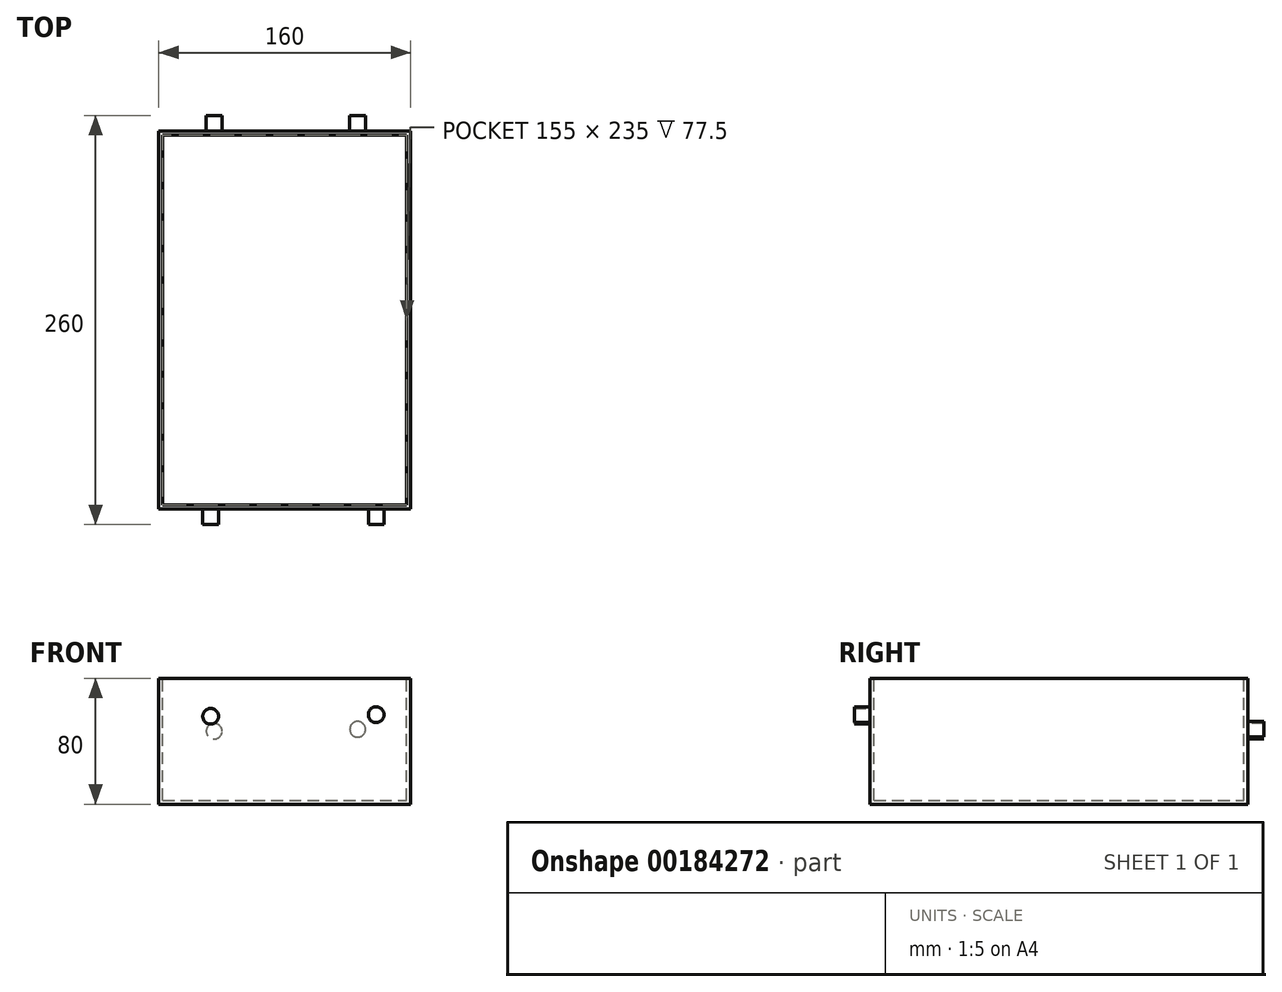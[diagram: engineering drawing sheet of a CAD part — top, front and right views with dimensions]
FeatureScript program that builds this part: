
annotation { "Feature Type Name" : "Feature", "Feature Type Description" : "" }
export const myFeature = defineFeature(function(context is Context, id is Id, definition is map)
    precondition{}
    {
        {
            var Q0;
            Q0=qCreatedBy(makeId("Front.planeOp"),FACE);
            var sketch = newSketch(context, id + "F0", { "sketchPlane" : qUnion([Q0])});
            skLineSegment(sketch, "E0.bottom", {"start": v(-80, -40) * mm, "end": v(80, -40) * mm});
            skLineSegment(sketch, "E0.top", {"start": v(-80, 40) * mm, "end": v(80, 40) * mm});
            skLineSegment(sketch, "E0.left", {"start": v(-80, -40) * mm, "end": v(-80, 40) * mm});
            skLineSegment(sketch, "E0.right", {"start": v(80, -40) * mm, "end": v(80, 40) * mm});
            skPoint(sketch, "E0.middle", {"position": v(0, 0) * mm});
            skSolve(sketch);
        }
        {
            var Q0;
            Q0=makeQuery(id+"F0.imprint","IMPRINT",FACE,{"disambiguationData":[TD([[makeQuery(id+"F0.imprint","IMPRINT",EDGE,{"derivedFrom":sQuery(id+"F0.wireOp",EDGE,"E0.bottom")}),1.0]])]});
            var sketch = newSketch(context, id + "F1", { "sketchPlane" : qUnion([Q0])});
            skSolve(sketch);
        }
        {
            var Q0;
            Q0=makeQuery(id+"F1.imprint","IMPRINT",FACE,{"disambiguationData":[TD([[makeQuery(id+"F1.imprint","IMPRINT",EDGE,{"derivedFrom":makeQuery(id+"F0.imprint","IMPRINT",EDGE,{"derivedFrom":sQuery(id+"F0.wireOp",EDGE,"E0.bottom")})}),1.0]])]});
            extrude(context, id + "F2", {"entities" : qUnion([Q0]), "endBound" : BoundingType.SYMMETRIC, "depth" : 240 * mm});
        }
        {
            var Q0;
            Q0=makeQuery(id+"F2.opExtrude","SWEPT_FACE",FACE,{"disambiguationData":[OSD([sQuery(id+"F0.wireOp",EDGE,"E0.left")])]});
            var sketch = newSketch(context, id + "F3", { "sketchPlane" : qUnion([Q0])});
            skSolve(sketch);
        }
        {
            var Q0;
            {var subQ0=sQuery(id+"F0.wireOp",EDGE,"E0.left");Q0=makeQuery(id+"F3.imprint","IMPRINT",FACE,{"disambiguationData":[TD([[makeQuery(id+"F3.imprint","IMPRINT",EDGE,{"derivedFrom":makeQuery(id+"F2.opExtrude","CAP_EDGE",EDGE,{"disambiguationData":[OSD([subQ0])],"isStart":true})}),-1.0]])]});}
            var sketch = newSketch(context, id + "F4", { "sketchPlane" : qUnion([Q0])});
            skSolve(sketch);
        }
        {
            var Q0;
            Q0=makeQuery(id+"F2.opExtrude","SWEPT_FACE",FACE,{"disambiguationData":[OSD([sQuery(id+"F0.wireOp",EDGE,"E0.top")])]});
            shell(context, id + "F5", {"entities" : qUnion([Q0]), "thickness" : 2.5 * mm});
        }
        {
            var Q0;
            Q0=makeQuery(id+"F2.opExtrude","CAP_FACE",FACE,{"disambiguationData":[OSD([sQuery(id+"F0.wireOp",EDGE,"E0.bottom"),sQuery(id+"F0.wireOp",EDGE,"E0.top"),sQuery(id+"F0.wireOp",EDGE,"E0.left"),sQuery(id+"F0.wireOp",EDGE,"E0.right")])],"isStart":false});
            var sketch = newSketch(context, id + "F6", { "sketchPlane" : qUnion([Q0])});
            skCircle(sketch, "E1", {"center": v(-47.01, 15.8) * mm, "radius": 5 * mm});
            skSolve(sketch);
        }
        {
            var Q0;
            Q0=makeQuery(id+"F6.imprint","IMPRINT",FACE,{"disambiguationData":[TD([[makeQuery(id+"F6.imprint","IMPRINT",EDGE,{"derivedFrom":sQuery(id+"F6.wireOp",EDGE,"E1")}),-1.0]])]});
            var sketch = newSketch(context, id + "F7", { "sketchPlane" : qUnion([Q0])});
            skCircle(sketch, "E2", {"center": v(58.14, 16.82) * mm, "radius": 5 * mm});
            skSolve(sketch);
        }
        {
            var Q0;
            Q0=makeQuery(id+"F7.imprint","IMPRINT",FACE,{"disambiguationData":[TD([[makeQuery(id+"F7.imprint","IMPRINT",EDGE,{"derivedFrom":sQuery(id+"F7.wireOp",EDGE,"E2")}),-1.0]])]});
            var sketch = newSketch(context, id + "F8", { "sketchPlane" : qUnion([Q0])});
            skSolve(sketch);
        }
        {
            var Q0;
            Q0=makeQuery(id+"F7.imprint","IMPRINT",FACE,{"disambiguationData":[TD([[makeQuery(id+"F7.imprint","IMPRINT",EDGE,{"derivedFrom":makeQuery(id+"F6.imprint","IMPRINT",EDGE,{"derivedFrom":sQuery(id+"F6.wireOp",EDGE,"E1")})}),1.0]])]});
            var Q1;
            Q1=makeQuery(id+"F7.imprint","IMPRINT",FACE,{"disambiguationData":[TD([[makeQuery(id+"F7.imprint","IMPRINT",EDGE,{"derivedFrom":sQuery(id+"F7.wireOp",EDGE,"E2")}),1.0]])]});
            var Q2;
            Q2=sQuery(id+"F6.wireOp",EDGE,"E1");
            var Q3;
            Q3=sQuery(id+"F7.wireOp",EDGE,"E2");
            extrude(context, id + "F9", {"entities" : qUnion([Q0, Q1]), "surfaceEntities" : qUnion([Q2, Q3]), "depth" : 10 * mm});
        }
        {
            var Q0;
            Q0=makeQuery(id+"F2.opExtrude","CAP_FACE",FACE,{"disambiguationData":[OSD([sQuery(id+"F0.wireOp",EDGE,"E0.bottom"),sQuery(id+"F0.wireOp",EDGE,"E0.top"),sQuery(id+"F0.wireOp",EDGE,"E0.left"),sQuery(id+"F0.wireOp",EDGE,"E0.right")])],"isStart":true});
            var sketch = newSketch(context, id + "F10", { "sketchPlane" : qUnion([Q0])});
            skCircle(sketch, "E3", {"center": v(-46.36, 7.55) * mm, "radius": 5 * mm});
            skSolve(sketch);
        }
        {
            var Q0;
            Q0=makeQuery(id+"F10.imprint","IMPRINT",FACE,{"disambiguationData":[TD([[makeQuery(id+"F10.imprint","IMPRINT",EDGE,{"derivedFrom":sQuery(id+"F10.wireOp",EDGE,"E3")}),-1.0]])]});
            var sketch = newSketch(context, id + "F11", { "sketchPlane" : qUnion([Q0])});
            skCircle(sketch, "E4", {"center": v(44.78, 6.32) * mm, "radius": 5 * mm});
            skSolve(sketch);
        }
        {
            var Q0;
            Q0=makeQuery(id+"F11.imprint","IMPRINT",FACE,{"disambiguationData":[TD([[makeQuery(id+"F11.imprint","IMPRINT",EDGE,{"derivedFrom":makeQuery(id+"F10.imprint","IMPRINT",EDGE,{"derivedFrom":sQuery(id+"F10.wireOp",EDGE,"E3")})}),1.0]])]});
            var Q1;
            Q1=makeQuery(id+"F11.imprint","IMPRINT",FACE,{"disambiguationData":[TD([[makeQuery(id+"F11.imprint","IMPRINT",EDGE,{"derivedFrom":sQuery(id+"F11.wireOp",EDGE,"E4")}),1.0]])]});
            extrude(context, id + "F12", {"entities" : qUnion([Q0, Q1]), "operationType" : NewBodyOperationType.ADD, "depth" : 10 * mm});
        }
        {
            var Q0;
            Q0=sQuery(id+"F6.wireOp",EDGE,"E1");
            extrude(context, id + "F13", {"bodyType" : ToolBodyType.SURFACE, "surfaceEntities" : qUnion([Q0]), "endBound" : BoundingType.SYMMETRIC, "depth" : 10 * mm, "hasSecondDirection" : true, "secondDirectionBound" : SecondDirectionBoundingType.THROUGH_ALL, "secondDirectionOppositeDirection" : true, "secondDirectionDepth" : 248.2 * mm});
        }
        {
            var Q0;
            Q0=sQuery(id+"F7.wireOp",EDGE,"E2");
            extrude(context, id + "F14", {"bodyType" : ToolBodyType.SURFACE, "surfaceEntities" : qUnion([Q0]), "depth" : 10 * mm});
        }
    });
